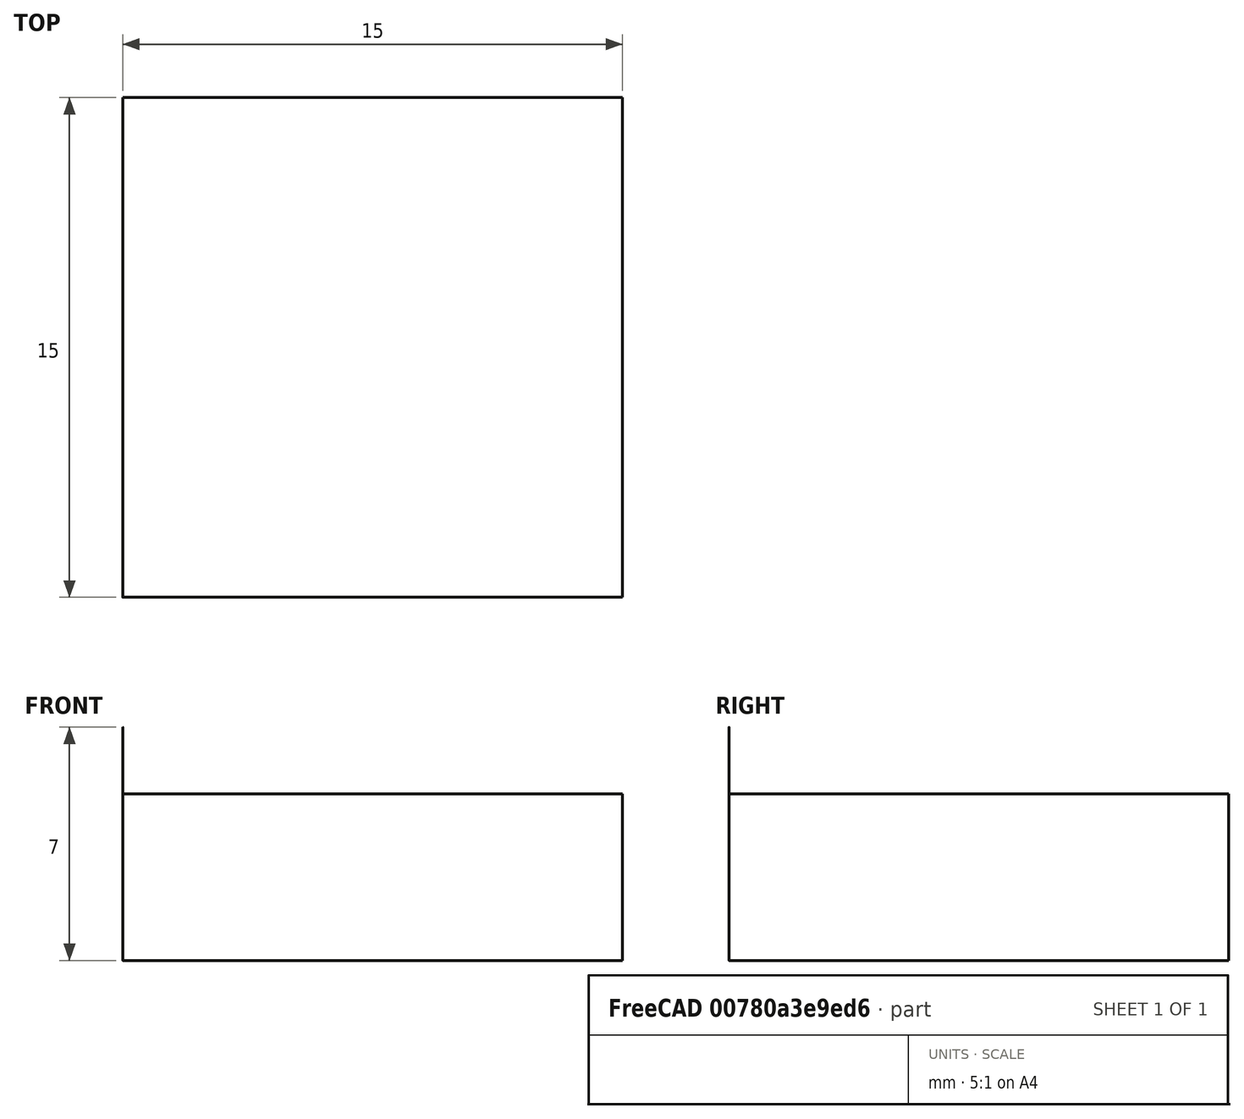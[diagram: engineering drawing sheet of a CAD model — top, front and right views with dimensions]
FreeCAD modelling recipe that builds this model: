
FCSTD DOCUMENT  (FreeCAD 1.0R39109 (Git))
Label: BoxWith5x5GridGrooves
License: All rights reserved
LicenseURL: https://en.wikipedia.org/wiki/All_rights_reserved
objects: Part::FeaturePython×3, App::DocumentObjectGroup×3, Path::FeaturePython×3, App::FeaturePython×2, Part::Feature×1, Sketcher::SketchObject×1, PartDesign::Revolution×1, PartDesign::Body×1
note: 11 computed .brp shape members not serialized (recipe doc carries the construction recipe); baked Part::Feature solids carry a one-line shape summary decoded from their .brp

FEATURE [Part::Feature] GridPocketBox
  shape: bbox 15 x 15 x 5 mm, 246 faces (baked)
FEATURE [App::FeaturePython] SetupSheet  # Path/CAM operation (typed FeaturePython)
  ClearanceHeightExpression = OpStockZMax+SetupSheet.ClearanceHeightOffset
  ClearanceHeightOffset = 5
  CoolantMode = 0
  CoolantModes = None | Flood | Mist
  FinalDepthExpression = OpFinalDepth
  HorizRapid = 0
  SafeHeightExpression = OpStockZMax+SetupSheet.SafeHeightOffset
  SafeHeightOffset = 3
  StartDepthExpression = OpStartDepth
  StepDownExpression = OpToolDiameter
  VertRapid = 0
FEATURE [Part::FeaturePython] Clone  label="Model-GridPocketBox"  # Draft clone (typed FeaturePython)
  AttacherType = Attacher::AttachEngine3D
  Fuse = false
  Objects = -> [GridPocketBox]
  PathResource = Model
  Scale = (1,1,1)
FEATURE [App::DocumentObjectGroup] Model
  Group = -> [Clone]
FEATURE [Part::FeaturePython] Stock  # WARN: FeaturePython — macro-defined, semantics opaque (R4)
  Base = -> Model
  ExtXneg = 0.001
  ExtXpos = 0.001
  ExtYneg = 0.001
  ExtYpos = 0.001
  ExtZneg = 0.001
  ExtZpos = 0.001
  StockType = FromBase
FEATURE [App::FeaturePython] PropertyBag  label="Attributes"  # WARN: FeaturePython — macro-defined, semantics opaque (R4)
  Chipload = 0
  CustomPropertyGroups = Attributes | Shape
  Diameter = 0.005
  Flutes = 0
  Length = 7
  Material = 0
  TipAngle = 119
FEATURE [Sketcher::SketchObject] Sketch
  ArcFitTolerance = 0
  AttachmentSupport = -> [XZ_Plane]
  FullyConstrained = true
  MakeInternals = false
  MapMode = 5
  Placement = pos=(0,0,0) rot=(1,0,0;1.5708rad)
  expr: Constraints[13] = <<Attributes>>.TipAngle
  expr: Constraints[14] = <<Attributes>>.Diameter
  expr: Constraints[15] = <<Attributes>>.Length
  sketch-geometry (7):
    g0: LineSegment StartX=0 StartY=7 StartZ=0 EndX=0 EndY=1.048e-13 EndZ=0
    g1: LineSegment StartX=0 StartY=1.051e-13 StartZ=0 EndX=0.0025 EndY=0.00147261 EndZ=0
    g2: LineSegment StartX=0.0025 StartY=0.00147261 StartZ=0 EndX=0.0025 EndY=7 EndZ=0
    g3: LineSegment StartX=0.0025 StartY=7 StartZ=0 EndX=0 EndY=7 EndZ=0
    g4: LineSegment [constr] StartX=0.0025 StartY=0.00147261 StartZ=0 EndX=-0.0025 EndY=0.00147261 EndZ=0
    g5: LineSegment [constr] StartX=-0.0025 StartY=0.00147261 StartZ=0 EndX=0 EndY=1.051e-13 EndZ=0
    g6: LineSegment [constr] StartX=0 StartY=1.051e-13 StartZ=0 EndX=0.0025 EndY=0.00147261 EndZ=0
  constraints (17):
    c: Vertical(g0)
    c: Coincident(g0,g1)
    c: Coincident(g1,g2)
    c: Vertical(g2)
    c: Coincident(g2,g3)
    c: Horizontal(g3)
    c: Coincident(g0,g3)
    c: Coincident(g4,g5)
    c: Coincident(g5,g6)
    c: Coincident(g6,g4)
    c: Coincident(g1,g4)
    c: Coincident(g5,g0)
    c: Symmetric(g4,g1,g0)
    c: Angle(g1,g5) = 2.07694
    c: DistanceX(g4,g4) = 0.005
    c: DistanceY(g0,g0) = 7
    c: Coincident(g0,g-1)
FEATURE [PartDesign::Revolution] Revolution
  AllowMultiFace = false
  Angle = 360
  Angle2 = 60
  Axis = (0,2e-16,1)
  Base = (0,0,0)
  Placement = pos=(0,0,0) rot=(1,0,0;1.5708rad)
  Profile = -> Sketch
  ReferenceAxis = -> Sketch [V_Axis]
  Reversed = true
  Suppressed = false
  Type = 0
FEATURE [PartDesign::Body] Body  label="Drill001"
  AllowCompound = false
  Group = -> [Sketch,Revolution,PropertyBag]
  Origin = -> Origin
  Tip = -> Revolution
FEATURE [Part::FeaturePython] ToolBit  label="Drill"  # Path/CAM toolbit (typed FeaturePython)
  BitBody = -> Body
  BitPropertyNames = Chipload | Diameter | Flutes | Length | Material | TipAngle
  BitShape = <path>
  Chipload = 0
  Diameter = 0.005
  Flutes = 0
  Length = 7
  Material = 0
  ShapeName = drill
  TipAngle = 119
FEATURE [Path::FeaturePython] TC__Default_Tool  label="TC: Default Tool"  # Path/CAM operation (typed FeaturePython)
  HorizFeed = 0
  HorizRapid = 0
  SpindleDir = 0
  SpindleSpeed = 0
  Tool = -> ToolBit
  ToolNumber = 1
  VertFeed = 0
  VertRapid = 0
  expr: HorizRapid = SetupSheet.HorizRapid
  expr: VertRapid = SetupSheet.VertRapid
FEATURE [App::DocumentObjectGroup] Tools
  Group = -> [TC__Default_Tool]
FEATURE [Path::FeaturePython] Pocket_Shape  # Path/CAM operation (typed FeaturePython)
  Active = true
  AreaParams:
    Tolerance = 1e-07
    FitArcs = True
    Simplify = False
    CleanDistance = 0.0
    Accuracy = 0.01
    Unit = 1.0
    MinArcPoints = 4
    MaxArcPoints = 100
    ClipperScale = 10000000.0
    Fill = 0
    Coplanar = 0
    Reorient = True
    Outline = False
    Explode = False
    OpenMode = 0
    Deflection = 0.01
    SubjectFill = 0
    ClipFill = 0
    Offset = 0.0
    ExtraPass = 0
    Stepover = 0.0
    LastStepover = 0.0
    JoinType = 0
    EndType = 0
    MiterLimit = 2.0
    RoundPrecision = 0.0
    PocketMode = 5
    ToolRadius = 0.0025
    PocketExtraOffset = 0.0
    PocketStepover = 0.0025
    PocketLastStepover = 0.0
    FromCenter = True
    Angle = 0.0
    AngleShift = 0.0
    Shift = 0.0
    Thicken = False
    SectionCount = -1
    Stepdown = 1.0
    SectionOffset = 0.0
    SectionTolerance = 1e-06
    SectionMode = 2
    Project = False
  Base = -> [Clone]
  ClearanceHeight = 10.001
  CoolantMode = 0
  CutMode = 0
  CycleTime = Cycletime Error
  ExtensionCorners = true
  ExtensionLengthDefault = 0.0025
  ExtraOffset = 0
  FinalDepth = 4.999
  FinishDepth = 0
  KeepToolDown = false
  MinTravel = false
  OffsetPattern = 3
  OpFinalDepth = 4.999
  OpStartDepth = 5.001
  OpStockZMax = 5.001
  OpStockZMin = -0.001
  OpToolDiameter = 0.005
  PathParams = {'orientation': 1, 'feedrate': 0.0, 'feedrate_v': 0.0, 'verbose': True, 'resume_height': 8.001000000000001, 'retraction': 10.001000000000001, 'return_end': True, 'preamble': False}
  PocketLastStepOver = 0
  SafeHeight = 8.001
  SplitArcs = false
  StartAt = 0
  StartDepth = 5.001
  StartPoint = (0,0,0)
  StepDown = 0.005
  StepOver = 50
  ToolController = -> TC__Default_Tool
  UseOutline = false
  UseRestMachining = false
  UseStartPoint = false
  ZigZagAngle = 0
  expr: ClearanceHeight = OpStockZMax + SetupSheet.ClearanceHeightOffset
  expr: ExtensionLengthDefault = OpToolDiameter / 2
  expr: FinalDepth = OpFinalDepth
  expr: SafeHeight = OpStockZMax + SetupSheet.SafeHeightOffset
  expr: StartDepth = OpStartDepth
  expr: StepDown = OpToolDiameter
FEATURE [App::DocumentObjectGroup] Operations
  Group = -> [Pocket_Shape]
FEATURE [Path::FeaturePython] Job  # Path/CAM operation (typed FeaturePython)
  CycleTime = 00:00:00
  Fixtures = G54
  GeometryTolerance = 0.01
  JobType = 0
  Model = -> Model
  Operations = -> Operations
  OrderOutputBy = 0
  PostProcessor = 14
  PostProcessorOutputFile = <userpath>/Desktop/laser-toolpath/freecad/laser5x5groovesgrid.gcode
  SetupSheet = -> SetupSheet
  SplitOutput = false
  Stock = -> Stock
  Tools = -> Tools
note: 1 file-system path scrubbed to <path> (originals preserved in the JSON sidecar)
